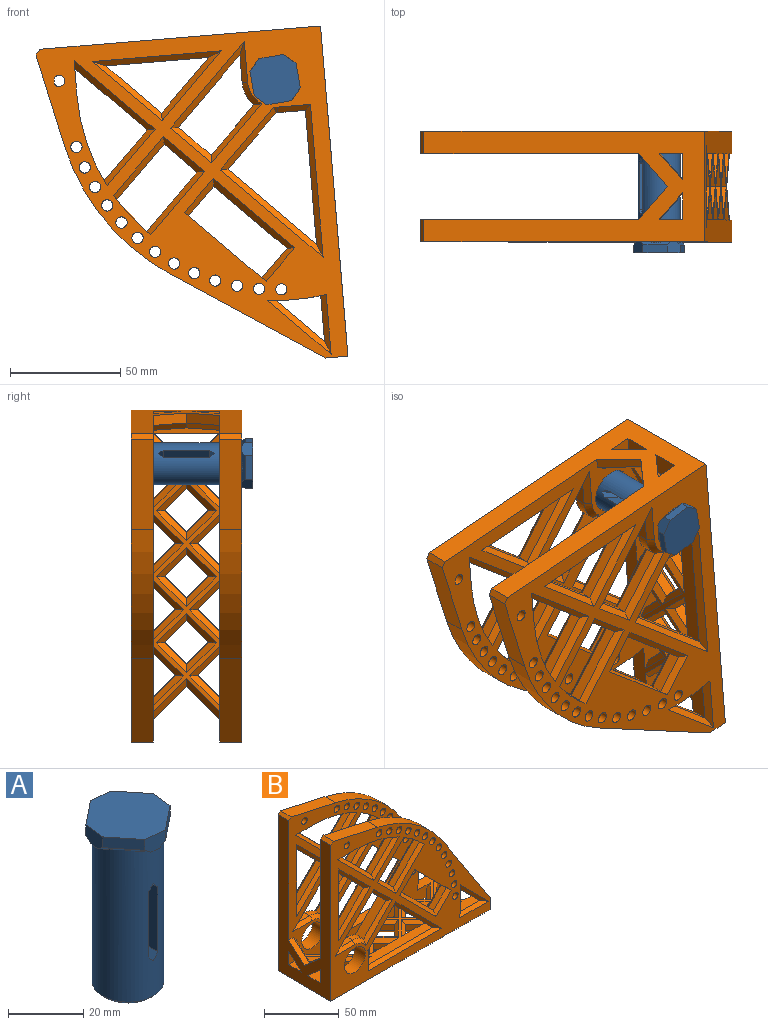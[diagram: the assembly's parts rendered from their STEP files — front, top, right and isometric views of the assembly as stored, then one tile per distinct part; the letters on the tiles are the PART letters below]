
ASSEMBLY  parts=2 mates=1
PART A: 26 faces, bbox 23.6x23.6x55 mm
  f0: plane 9x3.74mm, normal (0,0,-1), area 11.5mm2, adj f5,f19,f21,f24
  f1: plane 9x3.74mm, normal (0,0,-1), area 11.5mm2, adj f5,f20,f21,f22
  f2: plane 9x3.74mm, normal (0,0,-1), area 11.5mm2, adj f5,f18,f19,f25
  f3: plane 23.56x23.56mm, normal (0,0,1), area 400mm2, adj f14,f15,f16,f17,f22,f23,f24,f25
  f4: plane 9x3.74mm, normal (0,0,-1), area 11.5mm2, adj f5,f18,f20,f23
  f5: cylinder r=9.5mm len=49.39mm, axis (0,0,-1), area 2767mm2, adj f0,f1,f2,f4,f7,f8,f9,f10
  f6: plane 17x17mm, normal (0,0,-1), area 227mm2, adj f13
  f7: plane 19.01x2.11mm, normal (0.77,0,0.64), area 51.7mm2, adj f5,f8,f12
  f8: plane 19.01x2.11mm, normal (-0.77,0,0.64), area 51.7mm2, adj f5,f7,f9
  f9: plane 21x18.67mm, normal (-1,0,0), area 392.1mm2, adj f5,f8,f10
  f10: plane 19.01x2.11mm, normal (-0.77,0,-0.64), area 51.7mm2, adj f5,f9,f11
  f11: plane 19.01x2.11mm, normal (0.77,0,-0.64), area 51.7mm2, adj f5,f10,f12
  f12: plane 21x18.67mm, normal (1,0,0), area 392.1mm2, adj f5,f7,f11
  f13: cone r=9.5mm half-angle=45deg, axis (0,0,1), area 80mm2, adj f5,f6
  f14: plane 8.74x7.02mm, normal (-0.63,0.78,0), area 39.2mm2, adj f3,f19,f24,f25
  f15: plane 8.74x7.02mm, normal (0.63,-0.78,0), area 39.2mm2, adj f3,f20,f22,f23
  f16: plane 8.74x7.02mm, normal (-0.78,-0.63,0), area 39.2mm2, adj f3,f21,f22,f24
  f17: plane 8.74x7.02mm, normal (0.78,0.63,0), area 39.2mm2, adj f3,f18,f23,f25
  f18: plane 11.08x9.13mm, normal (0.55,0.44,-0.71), area 25mm2, adj f2,f4,f5,f17,f23,f25
  f19: plane 11.08x9.13mm, normal (-0.44,0.55,-0.71), area 25mm2, adj f0,f2,f5,f14,f24,f25
  f20: plane 11.08x9.13mm, normal (0.44,-0.55,-0.71), area 25mm2, adj f1,f4,f5,f15,f22,f23
  f21: plane 11.08x9.13mm, normal (-0.55,-0.44,-0.71), area 25mm2, adj f0,f1,f5,f16,f22,f24
  f22: plane 7.03x5mm, normal (-0.11,-0.99,0), area 32.2mm2, adj f1,f3,f15,f16,f20,f21
  f23: plane 7.03x5mm, normal (0.99,-0.11,0), area 32.2mm2, adj f3,f4,f15,f17,f18,f20
  f24: plane 7.03x5mm, normal (-0.99,0.11,0), area 32.2mm2, adj f0,f3,f14,f16,f19,f21
  f25: plane 7.03x5mm, normal (0.11,0.99,0), area 32.2mm2, adj f2,f3,f14,f17,f18,f19
PART B: 301 faces, bbox 150.1x50.1x129.5 mm
  f0: plane 27.07x10mm, normal (0,-1,0), area 217.7mm2, adj f3,f5,f6,f121,f122,f245,f246,f279
  f1: plane 150x129.45mm, normal (0,1,0), area 5860.7mm2, adj f2,f3,f4,f6,f9,f11,f12,f14
  f2: plane 10x10mm, normal (1,0,0), area 100mm2, adj f1,f6,f8,f16
  f3: plane 132.5x45mm, normal (0,0,1), area 1875.8mm2, adj f0,f1,f5,f9,f46,f48,f50,f51
  f4: plane 30x10mm, normal (0,0,1), area 268.3mm2, adj f1,f5,f11,f130,f138,f139,f229,f230
  f5: plane 150x129.45mm, normal (0,-1,0), area 5773.5mm2, adj f0,f3,f4,f6,f10,f11,f13,f17
  f6: plane 150x50mm, normal (0,0,-1), area 3957.4mm2, adj f0,f1,f2,f5,f7,f8,f9,f10
  f7: plane 150x129.45mm, normal (0,1,0), area 6563.1mm2, adj f6,f10,f11,f13,f17,f18,f19,f33
  f8: plane 150x129.45mm, normal (0,-1,0), area 6563.1mm2, adj f2,f6,f11,f12,f14,f15,f16,f20
  f9: plane 27.07x10mm, normal (0,1,0), area 217.7mm2, adj f1,f3,f6,f119,f120,f243,f244,f277
  f10: plane 10x10mm, normal (1,0,0), area 100mm2, adj f5,f6,f7,f17
  f11: plane 127.5x50mm, normal (-1,0,0), area 3122.6mm2, adj f1,f4,f5,f6,f7,f8,f98,f99
  f12: cylinder r=10mm len=20mm, axis (0,-1,0), area 628.3mm2, adj f1,f8
  f13: cylinder r=10mm len=20mm, axis (0,-1,0), area 628.3mm2, adj f5,f7
  f14: cylinder r=100mm len=61.96mm, axis (0,-1,0), area 773.3mm2, adj f1,f8,f15,f16
  f15: plane 41.88x10mm, normal (0.22,0,0.98), area 429.1mm2, adj f1,f8,f14,f99
  f16: plane 67.09x43.72mm, normal (0.84,0,0.55), area 800.8mm2, adj f1,f2,f8,f14
  f17: plane 67.09x43.72mm, normal (0.84,0,0.55), area 800.8mm2, adj f5,f7,f10,f19
  f18: plane 41.88x10mm, normal (0.22,0,0.98), area 429.1mm2, adj f5,f7,f19,f98
  f19: cylinder r=100mm len=61.96mm, axis (0,-1,0), area 773.3mm2, adj f5,f7,f17,f18
  f20: cylinder r=2.55mm len=10mm, axis (0,-1,0), area 160.2mm2, adj f1,f8
  f21: cylinder r=2.55mm len=10mm, axis (0,-1,0), area 160.2mm2, adj f1,f8
  f22: cylinder r=2.55mm len=10mm, axis (0,-1,0), area 160.2mm2, adj f1,f8
  f23: cylinder r=2.55mm len=10mm, axis (0,-1,0), area 160.2mm2, adj f1,f8
  f24: cylinder r=2.55mm len=10mm, axis (0,-1,0), area 160.2mm2, adj f1,f8
  f25: cylinder r=2.55mm len=10mm, axis (0,-1,0), area 160.2mm2, adj f1,f8
  f26: cylinder r=2.55mm len=10mm, axis (0,-1,0), area 160.2mm2, adj f1,f8
  f27: cylinder r=2.55mm len=10mm, axis (0,-1,0), area 160.2mm2, adj f1,f8
  f28: cylinder r=2.55mm len=10mm, axis (0,-1,0), area 160.2mm2, adj f1,f8
  f29: cylinder r=2.55mm len=10mm, axis (0,-1,0), area 160.2mm2, adj f1,f8
  f30: cylinder r=2.55mm len=10mm, axis (0,-1,0), area 160.2mm2, adj f1,f8
  f31: cylinder r=2.55mm len=10mm, axis (0,-1,0), area 160.2mm2, adj f1,f8
  f32: cylinder r=2.55mm len=10mm, axis (0,-1,0), area 160.2mm2, adj f1,f8
  f33: cylinder r=2.55mm len=10mm, axis (0,-1,0), area 160.2mm2, adj f5,f7
  f34: cylinder r=2.55mm len=10mm, axis (0,-1,0), area 160.2mm2, adj f5,f7
  f35: cylinder r=2.55mm len=10mm, axis (0,-1,0), area 160.2mm2, adj f5,f7
  f36: cylinder r=2.55mm len=10mm, axis (0,-1,0), area 160.2mm2, adj f5,f7
  f37: cylinder r=2.55mm len=10mm, axis (0,-1,0), area 160.2mm2, adj f5,f7
  f38: cylinder r=2.55mm len=10mm, axis (0,-1,0), area 160.2mm2, adj f5,f7
  f39: cylinder r=2.55mm len=10mm, axis (0,-1,0), area 160.2mm2, adj f5,f7
  f40: cylinder r=2.55mm len=10mm, axis (0,-1,0), area 160.2mm2, adj f5,f7
  f41: cylinder r=2.55mm len=10mm, axis (0,-1,0), area 160.2mm2, adj f5,f7
  f42: cylinder r=2.55mm len=10mm, axis (0,-1,0), area 160.2mm2, adj f5,f7
  f43: cylinder r=2.55mm len=10mm, axis (0,-1,0), area 160.2mm2, adj f5,f7
  f44: cylinder r=2.55mm len=10mm, axis (0,-1,0), area 160.2mm2, adj f5,f7
  f45: cylinder r=2.55mm len=10mm, axis (0,-1,0), area 160.2mm2, adj f5,f7
  f46: plane 12.5x5mm, normal (1,0,0), area 62.5mm2, adj f3,f49,f146,f150
  f47: plane 23.77x23.77mm, normal (0.71,0,-0.71), area 168.1mm2, adj f48,f49,f145,f151
  f48: plane 37.11x37.11mm, normal (-0.71,0,-0.71), area 262.4mm2, adj f3,f47,f144,f149
  f49: cylinder r=15mm len=5mm, axis (0,-1,0), area 4.2mm2, adj f46,f47,f147,f152
  f50: cylinder r=100mm len=26.73mm, axis (0,-1,0), area 216.5mm2, adj f1,f3,f8,f51,f153,f154,f155
  f51: plane 20.31x20.31mm, normal (-0.71,0,-0.71), area 143.6mm2, adj f3,f50,f153,f155
  f52: plane 23.36x23.36mm, normal (-0.71,0,-0.71), area 165.2mm2, adj f53,f54,f166,f168
  f53: plane 23.36x23.36mm, normal (-0.71,0,0.71), area 165.2mm2, adj f52,f54,f165,f169
  f54: plane 46.72x5mm, normal (1,0,0), area 233.6mm2, adj f52,f53,f167,f170
  f55: plane 34.27x34.27mm, normal (-0.71,0,-0.71), area 447.1mm2, adj f1,f8,f56,f58,f159,f161,f162,f164
  f56: plane 12.45x12.45mm, normal (-0.71,0,0.71), area 88mm2, adj f55,f57,f161,f164
  f57: plane 30.73x30.73mm, normal (0.71,0,0.71), area 217.3mm2, adj f56,f58,f160,f163
  f58: plane 12.45x12.45mm, normal (0.71,0,-0.71), area 88mm2, adj f55,f57,f159,f162
  f59: plane 30.43x30.43mm, normal (0.71,0,0.71), area 215.2mm2, adj f60,f62,f182,f184
  f60: plane 16.04x10mm, normal (0,0,-1), area 133.8mm2, adj f1,f8,f59,f61,f182,f184
  f61: cylinder r=90mm len=41.67mm, axis (0,-1,0), area 413.5mm2, adj f1,f8,f60,f62,f181,f183
  f62: plane 21.39x21.39mm, normal (-0.71,0,0.71), area 151.2mm2, adj f59,f61,f181,f183
  f63: cylinder r=90mm len=19.18mm, axis (0,-1,0), area 208.7mm2, adj f1,f8,f64,f66,f156,f158,f176,f178
  f64: plane 24.89x24.89mm, normal (-0.71,0,0.71), area 176mm2, adj f63,f65,f158,f178
  f65: plane 13.75x13.75mm, normal (0.71,0,0.71), area 97.2mm2, adj f64,f66,f157,f177
  f66: plane 23.39x23.39mm, normal (0.71,0,-0.71), area 165.4mm2, adj f63,f65,f156,f176
  f67: plane 12.5x5mm, normal (0,0,1), area 62.5mm2, adj f68,f71,f173,f299
  f68: plane 30.43x30.43mm, normal (0.71,0,-0.71), area 215.2mm2, adj f67,f69,f175,f179
  f69: plane 13.75x13.75mm, normal (-0.71,0,-0.71), area 97.2mm2, adj f68,f70,f174,f180
  f70: plane 24.61x24.61mm, normal (-0.71,0,0.71), area 229.8mm2, adj f1,f69,f71,f172,f180,f300
  f71: cylinder r=15mm len=10.61mm, axis (0,-1,0), area 58.9mm2, adj f67,f70,f171,f300
  f72: cylinder r=15mm len=5mm, axis (0,-1,0), area 4.2mm2, adj f73,f75,f189,f193
  f73: plane 12.5x5mm, normal (1,0,0), area 62.5mm2, adj f3,f72,f187,f192
  f74: plane 37.11x37.11mm, normal (-0.71,0,-0.71), area 262.4mm2, adj f3,f75,f186,f190
  f75: plane 23.77x23.77mm, normal (0.71,0,-0.71), area 168.1mm2, adj f72,f74,f188,f191
  f76: plane 20.31x20.31mm, normal (-0.71,0,-0.71), area 143.6mm2, adj f3,f77,f204,f206
  f77: cylinder r=100mm len=26.73mm, axis (0,-1,0), area 216.5mm2, adj f3,f5,f7,f76,f204,f205,f206
  f78: plane 46.72x5mm, normal (1,0,0), area 233.6mm2, adj f79,f80,f225,f228
  f79: plane 23.36x23.36mm, normal (-0.71,0,0.71), area 165.2mm2, adj f78,f80,f224,f226
  f80: plane 23.36x23.36mm, normal (-0.71,0,-0.71), area 165.2mm2, adj f78,f79,f223,f227
  f81: plane 12.45x12.45mm, normal (0.71,0,-0.71), area 88mm2, adj f82,f84,f207,f210
  f82: plane 30.73x30.73mm, normal (0.71,0,0.71), area 217.3mm2, adj f81,f83,f208,f211
  f83: plane 12.45x12.45mm, normal (-0.71,0,0.71), area 88mm2, adj f82,f84,f209,f212
  f84: plane 34.27x34.27mm, normal (-0.71,0,-0.71), area 447.1mm2, adj f5,f7,f81,f83,f207,f209,f210,f212
  f85: plane 21.39x21.39mm, normal (-0.71,0,0.71), area 151.2mm2, adj f86,f88,f220,f222
  f86: cylinder r=90mm len=41.67mm, axis (0,-1,0), area 413.5mm2, adj f5,f7,f85,f87,f220,f222
  f87: plane 16.04x10mm, normal (0,0,-1), area 133.8mm2, adj f5,f7,f86,f88,f219,f221
  f88: plane 30.43x30.43mm, normal (0.71,0,0.71), area 215.2mm2, adj f85,f87,f219,f221
  f89: plane 23.39x23.39mm, normal (0.71,0,-0.71), area 165.4mm2, adj f90,f92,f215,f216
  f90: plane 13.75x13.75mm, normal (0.71,0,0.71), area 97.2mm2, adj f89,f91,f214,f217
  f91: plane 24.89x24.89mm, normal (-0.71,0,0.71), area 176mm2, adj f90,f92,f213,f218
  f92: cylinder r=90mm len=19.18mm, axis (0,-1,0), area 208.7mm2, adj f5,f7,f89,f91,f213,f215,f216,f218
  f93: cylinder r=15mm len=10.61mm, axis (0,-1,0), area 58.9mm2, adj f94,f97,f197,f201
  f94: plane 21.07x21.07mm, normal (-0.71,0,0.71), area 149mm2, adj f93,f95,f195,f199
  f95: plane 13.75x13.75mm, normal (-0.71,0,-0.71), area 97.2mm2, adj f94,f96,f194,f200
  f96: plane 30.43x30.43mm, normal (0.71,0,-0.71), area 215.2mm2, adj f95,f97,f196,f202
  f97: plane 12.5x5mm, normal (0,0,1), area 62.5mm2, adj f93,f96,f198,f203
  f98: plane 10x2.44mm, normal (-0.63,0,0.78), area 31.3mm2, adj f5,f7,f11,f18
  f99: plane 10x2.44mm, normal (-0.63,0,0.78), area 31.3mm2, adj f1,f8,f11,f15
  f100: plane 10x10mm, normal (0.71,0.71,0), area 70.7mm2, adj f5,f101,f236,f269
  f101: plane 10x10mm, normal (-0.71,0.71,0), area 70.7mm2, adj f5,f100,f235,f270
  f102: plane 10x10mm, normal (-0.71,-0.71,0), area 70.7mm2, adj f103,f105,f241,f275
  f103: plane 10x10mm, normal (0.71,-0.71,0), area 70.7mm2, adj f102,f104,f239,f273
  f104: plane 10x10mm, normal (0.71,0.71,0), area 70.7mm2, adj f103,f105,f240,f274
  f105: plane 10x10mm, normal (-0.71,0.71,0), area 70.7mm2, adj f102,f104,f242,f276
  f106: plane 10x10mm, normal (0.71,-0.71,0), area 70.7mm2, adj f1,f107,f238,f271
  f107: plane 10x10mm, normal (-0.71,-0.71,0), area 70.7mm2, adj f1,f106,f237,f272
  f108: plane 10x10mm, normal (-0.71,-0.71,0), area 70.7mm2, adj f109,f111,f257,f296
  f109: plane 10x10mm, normal (0.71,-0.71,0), area 70.7mm2, adj f108,f110,f255,f294
  f110: plane 10x10mm, normal (0.71,0.71,0), area 70.7mm2, adj f109,f111,f256,f293
  f111: plane 10x10mm, normal (-0.71,0.71,0), area 70.7mm2, adj f108,f110,f258,f295
  f112: plane 27.07x10mm, normal (0,-1,0), area 217.7mm2, adj f3,f6,f113,f114,f253,f254,f291,f292
  f113: plane 10x10mm, normal (0.71,0.71,0), area 70.7mm2, adj f112,f114,f253,f291
  f114: plane 10x10mm, normal (-0.71,0.71,0), area 70.7mm2, adj f112,f113,f254,f292
  f115: plane 10x10mm, normal (0.71,-0.71,0), area 70.7mm2, adj f1,f116,f260,f285
  f116: plane 10x10mm, normal (-0.71,-0.71,0), area 70.7mm2, adj f1,f115,f259,f286
  f117: plane 10x10mm, normal (0.71,0.71,0), area 70.7mm2, adj f5,f118,f262,f288
  f118: plane 10x10mm, normal (-0.71,0.71,0), area 70.7mm2, adj f5,f117,f261,f289
  f119: plane 10x10mm, normal (-0.71,-0.71,0), area 70.7mm2, adj f9,f120,f243,f278
  f120: plane 10x10mm, normal (0.71,-0.71,0), area 70.7mm2, adj f9,f119,f244,f277
  f121: plane 10x10mm, normal (-0.71,0.71,0), area 70.7mm2, adj f0,f122,f246,f280
  f122: plane 10x10mm, normal (0.71,0.71,0), area 70.7mm2, adj f0,f121,f245,f279
  f123: plane 10x10mm, normal (0.71,-0.71,0), area 70.7mm2, adj f124,f125,f252,f265
  f124: plane 27.07x10mm, normal (0,1,0), area 217.7mm2, adj f3,f6,f123,f125,f251,f252,f265,f266
  f125: plane 10x10mm, normal (-0.71,-0.71,0), area 70.7mm2, adj f123,f124,f251,f266
  f126: plane 10x10mm, normal (0.71,0.71,0), area 70.7mm2, adj f127,f129,f248,f284
  f127: plane 10x10mm, normal (-0.71,0.71,0), area 70.7mm2, adj f126,f128,f250,f282
  f128: plane 10x10mm, normal (-0.71,-0.71,0), area 70.7mm2, adj f127,f129,f249,f281
  f129: plane 10x10mm, normal (0.71,-0.71,0), area 70.7mm2, adj f126,f128,f247,f283
  f130: plane 37.07x10mm, normal (1,0,0), area 308.8mm2, adj f1,f4,f5,f6,f131,f132,f263,f264
  f131: plane 15x15mm, normal (-0.71,0.71,0), area 106.1mm2, adj f130,f132,f263,f298
  f132: plane 15x15mm, normal (-0.71,-0.71,0), area 106.1mm2, adj f130,f131,f264,f297
  f133: cylinder r=100mm len=10mm, axis (0,-1,0), area 25.7mm2, adj f1,f8,f134
  f134: cylinder r=2.55mm len=10mm, axis (0,-1,0), area 133.3mm2, adj f1,f8,f133
  f135: cylinder r=2.55mm len=10mm, axis (0,-1,0), area 133.3mm2, adj f5,f7,f136
  f136: cylinder r=100mm len=10mm, axis (0,-1,0), area 25.7mm2, adj f5,f7,f135
  f137: plane 15x13.23mm, normal (0,-0.66,0.75), area 90mm2, adj f5,f11,f140,f232
  f138: plane 12.1x10.67mm, normal (0,0.66,-0.75), area 72.6mm2, adj f4,f5,f11,f230
  f139: plane 12.1x10.67mm, normal (0,-0.66,-0.75), area 72.6mm2, adj f1,f4,f11,f229
  f140: plane 15x13.23mm, normal (0,0.66,0.75), area 90mm2, adj f1,f11,f137,f231
  f141: plane 30x15.9mm, normal (1,0,0), area 80mm2, adj f1,f5,f229,f230,f231,f232
  f142: plane 15x15mm, normal (0.71,-0.71,0), area 106.1mm2, adj f5,f143,f233,f267
  f143: plane 15x15mm, normal (0.71,0.71,0), area 106.1mm2, adj f1,f142,f234,f268
  f144: plane 40.64x40.64mm, normal (-0.5,0.71,-0.5), area 194.4mm2, adj f1,f3,f48,f145
  f145: plane 27.39x26.46mm, normal (0.5,0.71,-0.5), area 125.3mm2, adj f1,f47,f144,f147
  f146: plane 15x2.5mm, normal (0.71,0.71,0), area 48.6mm2, adj f1,f46,f147,f287
  f147: cone r=12.5mm half-angle=45deg, axis (0,-1,0), area 4.7mm2, adj f1,f49,f145,f146
  f148: plane 69.39x2.5mm, normal (0,-0.71,0.71), area 230.3mm2, adj f3,f8,f149,f150
  f149: plane 43.14x43.14mm, normal (-0.5,-0.71,-0.5), area 200.6mm2, adj f8,f48,f148,f151
  f150: plane 15x2.5mm, normal (0.71,-0.71,0), area 48.6mm2, adj f8,f46,f148,f152
  f151: plane 27.39x26.46mm, normal (0.5,-0.71,-0.5), area 125.3mm2, adj f8,f47,f149,f152
  f152: cone r=12.5mm half-angle=45deg, axis (0,1,0), area 4.7mm2, adj f8,f49,f150,f151
  f153: plane 26.76x26.76mm, normal (-0.5,-0.71,-0.5), area 117.5mm2, adj f8,f50,f51,f154
  f154: plane 27.17x2.5mm, normal (0,-0.71,0.71), area 84.7mm2, adj f3,f8,f50,f153
  f155: plane 24.26x24.26mm, normal (-0.5,0.71,-0.5), area 111.3mm2, adj f1,f3,f50,f51
  f156: plane 26.93x24.74mm, normal (0.5,0.71,-0.5), area 120.3mm2, adj f1,f63,f66,f157
  f157: plane 17.29x17.29mm, normal (0.5,0.71,0.5), area 77.6mm2, adj f1,f65,f156,f158
  f158: plane 28.43x26.63mm, normal (-0.5,0.71,0.5), area 128.8mm2, adj f1,f63,f64,f157
  f159: plane 15.98x14.21mm, normal (0.5,0.71,-0.5), area 66.6mm2, adj f1,f55,f58,f160
  f160: plane 34.27x34.27mm, normal (0.5,0.71,0.5), area 162.5mm2, adj f1,f57,f159,f161
  f161: plane 15.98x14.21mm, normal (-0.5,0.71,0.5), area 66.6mm2, adj f1,f55,f56,f160
  f162: plane 15.98x14.21mm, normal (0.5,-0.71,-0.5), area 66.6mm2, adj f8,f55,f58,f163
  f163: plane 34.27x34.27mm, normal (0.5,-0.71,0.5), area 162.5mm2, adj f8,f57,f162,f164
  f164: plane 15.98x14.21mm, normal (-0.5,-0.71,0.5), area 66.6mm2, adj f8,f55,f56,f163
  f165: plane 29.39x29.39mm, normal (-0.5,-0.71,0.5), area 131.9mm2, adj f8,f53,f166,f167
  f166: plane 29.39x29.39mm, normal (-0.5,-0.71,-0.5), area 131.9mm2, adj f8,f52,f165,f167
  f167: plane 58.79x2.5mm, normal (0.71,-0.71,0), area 186.5mm2, adj f8,f54,f165,f166
  f168: plane 29.39x29.39mm, normal (-0.5,0.71,-0.5), area 131.9mm2, adj f1,f52,f169,f170
  f169: plane 29.39x29.39mm, normal (-0.5,0.71,0.5), area 131.9mm2, adj f1,f53,f168,f170
  f170: plane 58.79x2.5mm, normal (0.71,0.71,0), area 186.5mm2, adj f1,f54,f168,f169
  f171: cone r=12.5mm half-angle=45deg, axis (0,1,0), area 42.6mm2, adj f8,f71,f172,f173
  f172: plane 24.79x24.79mm, normal (-0.5,-0.71,0.5), area 114.5mm2, adj f8,f70,f171,f174
  f173: plane 18.54x2.5mm, normal (0,-0.71,0.71), area 54.9mm2, adj f8,f67,f171,f175
  f174: plane 17.29x17.29mm, normal (-0.5,-0.71,-0.5), area 77.6mm2, adj f8,f69,f172,f175
  f175: plane 36.46x36.46mm, normal (0.5,-0.71,-0.5), area 167.2mm2, adj f8,f68,f173,f174
  f176: plane 26.93x24.74mm, normal (0.5,-0.71,-0.5), area 120.3mm2, adj f8,f63,f66,f177
  f177: plane 17.29x17.29mm, normal (0.5,-0.71,0.5), area 77.6mm2, adj f8,f65,f176,f178
  f178: plane 28.43x26.63mm, normal (-0.5,-0.71,0.5), area 128.8mm2, adj f8,f63,f64,f177
  f179: plane 36.46x36.46mm, normal (0.5,0.71,-0.5), area 167.2mm2, adj f1,f68,f180,f299
  f180: plane 17.29x15.52mm, normal (-0.5,0.71,-0.5), area 73.2mm2, adj f1,f69,f70,f179
  f181: plane 24.93x23.74mm, normal (-0.5,-0.71,0.5), area 112.8mm2, adj f8,f61,f62,f182
  f182: plane 33.96x33.96mm, normal (0.5,-0.71,0.5), area 161mm2, adj f8,f59,f60,f181
  f183: plane 24.93x23.74mm, normal (-0.5,0.71,0.5), area 112.8mm2, adj f1,f61,f62,f184
  f184: plane 33.96x33.96mm, normal (0.5,0.71,0.5), area 161mm2, adj f1,f59,f60,f183
  f185: plane 69.39x2.5mm, normal (0,0.71,0.71), area 230.3mm2, adj f3,f7,f186,f187
  f186: plane 43.14x43.14mm, normal (-0.5,0.71,-0.5), area 200.6mm2, adj f7,f74,f185,f188
  f187: plane 15x2.5mm, normal (0.71,0.71,0), area 48.6mm2, adj f7,f73,f185,f189
  f188: plane 27.39x26.46mm, normal (0.5,0.71,-0.5), area 125.3mm2, adj f7,f75,f186,f189
  f189: cone r=15mm half-angle=45deg, axis (0,-1,0), area 4.7mm2, adj f7,f72,f187,f188
  f190: plane 40.64x40.64mm, normal (-0.5,-0.71,-0.5), area 194.4mm2, adj f3,f5,f74,f191
  f191: plane 27.39x26.46mm, normal (0.5,-0.71,-0.5), area 125.3mm2, adj f5,f75,f190,f193
  f192: plane 15x2.5mm, normal (0.71,-0.71,0), area 48.6mm2, adj f5,f73,f193,f290
  f193: cone r=15mm half-angle=45deg, axis (0,1,0), area 4.7mm2, adj f5,f72,f191,f192
  f194: plane 17.29x17.29mm, normal (-0.5,-0.71,-0.5), area 77.6mm2, adj f5,f95,f195,f196
  f195: plane 24.79x24.79mm, normal (-0.5,-0.71,0.5), area 114.5mm2, adj f5,f94,f194,f197
  f196: plane 36.46x36.46mm, normal (0.5,-0.71,-0.5), area 167.2mm2, adj f5,f96,f194,f198
  f197: cone r=15mm half-angle=45deg, axis (0,1,0), area 42.6mm2, adj f5,f93,f195,f198
  f198: plane 18.54x2.5mm, normal (0,-0.71,0.71), area 54.9mm2, adj f5,f97,f196,f197
  f199: plane 24.79x24.79mm, normal (-0.5,0.71,0.5), area 114.5mm2, adj f7,f94,f200,f201
  f200: plane 17.29x17.29mm, normal (-0.5,0.71,-0.5), area 77.6mm2, adj f7,f95,f199,f202
  f201: cone r=15mm half-angle=45deg, axis (0,-1,0), area 42.6mm2, adj f7,f93,f199,f203
  f202: plane 36.46x36.46mm, normal (0.5,0.71,-0.5), area 167.2mm2, adj f7,f96,f200,f203
  f203: plane 18.54x2.5mm, normal (0,0.71,0.71), area 54.9mm2, adj f7,f97,f201,f202
  f204: plane 26.76x26.76mm, normal (-0.5,0.71,-0.5), area 117.5mm2, adj f7,f76,f77,f205
  f205: plane 27.17x2.5mm, normal (0,0.71,0.71), area 84.7mm2, adj f3,f7,f77,f204
  f206: plane 24.26x24.26mm, normal (-0.5,-0.71,-0.5), area 111.3mm2, adj f3,f5,f76,f77
  f207: plane 15.98x14.21mm, normal (0.5,-0.71,-0.5), area 66.6mm2, adj f5,f81,f84,f208
  f208: plane 34.27x34.27mm, normal (0.5,-0.71,0.5), area 162.5mm2, adj f5,f82,f207,f209
  f209: plane 15.98x14.21mm, normal (-0.5,-0.71,0.5), area 66.6mm2, adj f5,f83,f84,f208
  f210: plane 15.98x14.21mm, normal (0.5,0.71,-0.5), area 66.6mm2, adj f7,f81,f84,f211
  f211: plane 34.27x34.27mm, normal (0.5,0.71,0.5), area 162.5mm2, adj f7,f82,f210,f212
  f212: plane 15.98x14.21mm, normal (-0.5,0.71,0.5), area 66.6mm2, adj f7,f83,f84,f211
  f213: plane 28.43x26.63mm, normal (-0.5,-0.71,0.5), area 128.8mm2, adj f5,f91,f92,f214
  f214: plane 17.29x17.29mm, normal (0.5,-0.71,0.5), area 77.6mm2, adj f5,f90,f213,f215
  f215: plane 26.93x24.74mm, normal (0.5,-0.71,-0.5), area 120.3mm2, adj f5,f89,f92,f214
  f216: plane 26.93x24.74mm, normal (0.5,0.71,-0.5), area 120.3mm2, adj f7,f89,f92,f217
  f217: plane 17.29x17.29mm, normal (0.5,0.71,0.5), area 77.6mm2, adj f7,f90,f216,f218
  f218: plane 28.43x26.63mm, normal (-0.5,0.71,0.5), area 128.8mm2, adj f7,f91,f92,f217
  f219: plane 33.96x33.96mm, normal (0.5,-0.71,0.5), area 161mm2, adj f5,f87,f88,f220
  f220: plane 24.93x23.74mm, normal (-0.5,-0.71,0.5), area 112.8mm2, adj f5,f85,f86,f219
  f221: plane 33.96x33.96mm, normal (0.5,0.71,0.5), area 161mm2, adj f7,f87,f88,f222
  f222: plane 24.93x23.74mm, normal (-0.5,0.71,0.5), area 112.8mm2, adj f7,f85,f86,f221
  f223: plane 29.39x29.39mm, normal (-0.5,-0.71,-0.5), area 131.9mm2, adj f5,f80,f224,f225
  f224: plane 29.39x29.39mm, normal (-0.5,-0.71,0.5), area 131.9mm2, adj f5,f79,f223,f225
  f225: plane 58.79x2.5mm, normal (0.71,-0.71,0), area 186.5mm2, adj f5,f78,f223,f224
  f226: plane 29.39x29.39mm, normal (-0.5,0.71,0.5), area 131.9mm2, adj f7,f79,f227,f228
  f227: plane 29.39x29.39mm, normal (-0.5,0.71,-0.5), area 131.9mm2, adj f7,f80,f226,f228
  f228: plane 58.79x2.5mm, normal (0.71,0.71,0), area 186.5mm2, adj f7,f78,f226,f227
  f229: plane 15x14mm, normal (0.71,-0.47,-0.53), area 65.4mm2, adj f1,f4,f139,f141,f230
  f230: plane 15x14mm, normal (0.71,0.47,-0.53), area 65.4mm2, adj f4,f5,f138,f141,f229
  f231: plane 16.56x15mm, normal (0.71,0.47,0.53), area 70.7mm2, adj f1,f140,f141,f232
  f232: plane 16.56x15mm, normal (0.71,-0.47,0.53), area 70.7mm2, adj f5,f137,f141,f231
  f233: plane 18.54x15mm, normal (0.5,-0.5,-0.71), area 75mm2, adj f5,f6,f142,f234
  f234: plane 18.54x15mm, normal (0.5,0.5,-0.71), area 75mm2, adj f1,f6,f143,f233
  f235: plane 13.54x13.54mm, normal (-0.5,0.5,-0.71), area 58.8mm2, adj f5,f6,f101,f236
  f236: plane 13.54x13.54mm, normal (0.5,0.5,-0.71), area 58.8mm2, adj f5,f6,f100,f235
  f237: plane 13.54x13.54mm, normal (-0.5,-0.5,-0.71), area 58.8mm2, adj f1,f6,f107,f238
  f238: plane 13.54x13.54mm, normal (0.5,-0.5,-0.71), area 58.8mm2, adj f1,f6,f106,f237
  f239: plane 13.54x13.54mm, normal (0.5,-0.5,-0.71), area 58.8mm2, adj f6,f103,f240,f241
  f240: plane 13.54x13.54mm, normal (0.5,0.5,-0.71), area 58.8mm2, adj f6,f104,f239,f242
  f241: plane 13.54x13.54mm, normal (-0.5,-0.5,-0.71), area 58.8mm2, adj f6,f102,f239,f242
  f242: plane 13.54x13.54mm, normal (-0.5,0.5,-0.71), area 58.8mm2, adj f6,f105,f240,f241
  f243: plane 13.54x13.54mm, normal (-0.5,-0.5,-0.71), area 58.8mm2, adj f6,f9,f119,f244
  f244: plane 13.54x13.54mm, normal (0.5,-0.5,-0.71), area 58.8mm2, adj f6,f9,f120,f243
  f245: plane 13.54x13.54mm, normal (0.5,0.5,-0.71), area 58.8mm2, adj f0,f6,f122,f246
  f246: plane 13.54x13.54mm, normal (-0.5,0.5,-0.71), area 58.8mm2, adj f0,f6,f121,f245
  f247: plane 13.54x13.54mm, normal (0.5,-0.5,-0.71), area 58.8mm2, adj f6,f129,f248,f249
  f248: plane 13.54x13.54mm, normal (0.5,0.5,-0.71), area 58.8mm2, adj f6,f126,f247,f250
  f249: plane 13.54x13.54mm, normal (-0.5,-0.5,-0.71), area 58.8mm2, adj f6,f128,f247,f250
  f250: plane 13.54x13.54mm, normal (-0.5,0.5,-0.71), area 58.8mm2, adj f6,f127,f248,f249
  f251: plane 13.54x13.54mm, normal (-0.5,-0.5,-0.71), area 58.8mm2, adj f6,f124,f125,f252
  f252: plane 13.54x13.54mm, normal (0.5,-0.5,-0.71), area 58.8mm2, adj f6,f123,f124,f251
  f253: plane 13.54x13.54mm, normal (0.5,0.5,-0.71), area 58.8mm2, adj f6,f112,f113,f254
  f254: plane 13.54x13.54mm, normal (-0.5,0.5,-0.71), area 58.8mm2, adj f6,f112,f114,f253
  f255: plane 13.54x13.54mm, normal (0.5,-0.5,-0.71), area 58.8mm2, adj f6,f109,f256,f257
  f256: plane 13.54x13.54mm, normal (0.5,0.5,-0.71), area 58.8mm2, adj f6,f110,f255,f258
  f257: plane 13.54x13.54mm, normal (-0.5,-0.5,-0.71), area 58.8mm2, adj f6,f108,f255,f258
  f258: plane 13.54x13.54mm, normal (-0.5,0.5,-0.71), area 58.8mm2, adj f6,f111,f256,f257
  f259: plane 13.54x13.54mm, normal (-0.5,-0.5,-0.71), area 58.8mm2, adj f1,f6,f116,f260
  f260: plane 13.54x13.54mm, normal (0.5,-0.5,-0.71), area 58.8mm2, adj f1,f6,f115,f259
  f261: plane 13.54x13.54mm, normal (-0.5,0.5,-0.71), area 58.8mm2, adj f5,f6,f118,f262
  f262: plane 13.54x13.54mm, normal (0.5,0.5,-0.71), area 58.8mm2, adj f5,f6,f117,f261
  f263: plane 18.54x18.54mm, normal (-0.5,0.5,-0.71), area 83.8mm2, adj f6,f130,f131,f264
  f264: plane 18.54x18.54mm, normal (-0.5,-0.5,-0.71), area 83.8mm2, adj f6,f130,f132,f263
  f265: plane 13.54x13.54mm, normal (0.5,-0.5,0.71), area 58.8mm2, adj f3,f123,f124,f266
  f266: plane 13.54x13.54mm, normal (-0.5,-0.5,0.71), area 58.8mm2, adj f3,f124,f125,f265
  f267: plane 18.54x15mm, normal (0.5,-0.5,0.71), area 75mm2, adj f3,f5,f142,f268
  f268: plane 18.54x15mm, normal (0.5,0.5,0.71), area 75mm2, adj f1,f3,f143,f267
  f269: plane 13.54x13.54mm, normal (0.5,0.5,0.71), area 58.8mm2, adj f3,f5,f100,f270
  f270: plane 13.54x13.54mm, normal (-0.5,0.5,0.71), area 58.8mm2, adj f3,f5,f101,f269
  f271: plane 13.54x13.54mm, normal (0.5,-0.5,0.71), area 58.8mm2, adj f1,f3,f106,f272
  f272: plane 13.54x13.54mm, normal (-0.5,-0.5,0.71), area 58.8mm2, adj f1,f3,f107,f271
  f273: plane 13.54x13.54mm, normal (0.5,-0.5,0.71), area 58.8mm2, adj f3,f103,f274,f275
  f274: plane 13.54x13.54mm, normal (0.5,0.5,0.71), area 58.8mm2, adj f3,f104,f273,f276
  f275: plane 13.54x13.54mm, normal (-0.5,-0.5,0.71), area 58.8mm2, adj f3,f102,f273,f276
  f276: plane 13.54x13.54mm, normal (-0.5,0.5,0.71), area 58.8mm2, adj f3,f105,f274,f275
  f277: plane 13.54x13.54mm, normal (0.5,-0.5,0.71), area 58.8mm2, adj f3,f9,f120,f278
  f278: plane 13.54x13.54mm, normal (-0.5,-0.5,0.71), area 58.8mm2, adj f3,f9,f119,f277
  f279: plane 13.54x13.54mm, normal (0.5,0.5,0.71), area 58.8mm2, adj f0,f3,f122,f280
  f280: plane 13.54x13.54mm, normal (-0.5,0.5,0.71), area 58.8mm2, adj f0,f3,f121,f279
  f281: plane 13.54x13.54mm, normal (-0.5,-0.5,0.71), area 58.8mm2, adj f3,f128,f282,f283
  f282: plane 13.54x13.54mm, normal (-0.5,0.5,0.71), area 58.8mm2, adj f3,f127,f281,f284
  f283: plane 13.54x13.54mm, normal (0.5,-0.5,0.71), area 58.8mm2, adj f3,f129,f281,f284
  f284: plane 13.54x13.54mm, normal (0.5,0.5,0.71), area 58.8mm2, adj f3,f126,f282,f283
  f285: plane 13.54x13.54mm, normal (0.5,-0.5,0.71), area 58.8mm2, adj f1,f3,f115,f286
  f286: plane 16.04x16.04mm, normal (-0.5,-0.5,0.71), area 65.1mm2, adj f3,f116,f285,f287
  f287: plane 11.04x2.5mm, normal (0,0.71,0.71), area 23.9mm2, adj f1,f3,f146,f286
  f288: plane 13.54x13.54mm, normal (0.5,0.5,0.71), area 58.8mm2, adj f3,f5,f117,f289
  f289: plane 16.04x16.04mm, normal (-0.5,0.5,0.71), area 65.1mm2, adj f3,f118,f288,f290
  f290: plane 11.04x2.5mm, normal (0,-0.71,0.71), area 23.9mm2, adj f3,f5,f192,f289
  f291: plane 13.54x13.54mm, normal (0.5,0.5,0.71), area 58.8mm2, adj f3,f112,f113,f292
  f292: plane 13.54x13.54mm, normal (-0.5,0.5,0.71), area 58.8mm2, adj f3,f112,f114,f291
  f293: plane 13.54x13.54mm, normal (0.5,0.5,0.71), area 58.8mm2, adj f3,f110,f294,f295
  f294: plane 13.54x13.54mm, normal (0.5,-0.5,0.71), area 58.8mm2, adj f3,f109,f293,f296
  f295: plane 13.54x13.54mm, normal (-0.5,0.5,0.71), area 58.8mm2, adj f3,f111,f293,f296
  f296: plane 13.54x13.54mm, normal (-0.5,-0.5,0.71), area 58.8mm2, adj f3,f108,f294,f295
  f297: plane 18.54x15mm, normal (-0.5,-0.5,0.71), area 75mm2, adj f3,f5,f132,f298
  f298: plane 18.54x15mm, normal (-0.5,0.5,0.71), area 75mm2, adj f1,f3,f131,f297
  f299: plane 18.54x2.5mm, normal (0,0.71,0.71), area 54.9mm2, adj f1,f67,f179,f300
  f300: cone r=12.5mm half-angle=45deg, axis (0,-1,0), area 38.2mm2, adj f1,f70,f71,f299
PLACE A rot(axis=(0.77,-0.45,0.45),105deg) t=(-56.4,35.84,13.01)mm
PLACE B rot(axis=(0.74,0,-0.68),180deg) t=(-29.64,10.84,-37.45)mm
MATE cylindrical A.f5 <-> B.f12  axis (0,1,0) through (-56.4,35.84,13.01)mm
